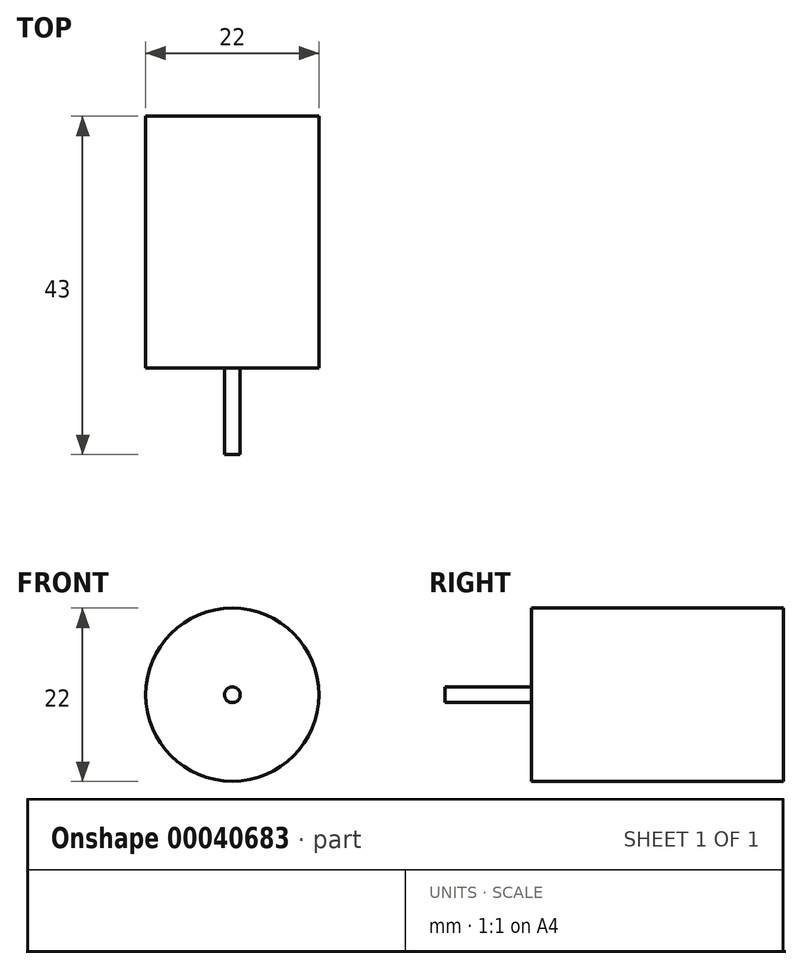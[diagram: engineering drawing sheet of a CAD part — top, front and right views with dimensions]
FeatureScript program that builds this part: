
annotation { "Feature Type Name" : "Feature", "Feature Type Description" : "" }
export const myFeature = defineFeature(function(context is Context, id is Id, definition is map)
    precondition{}
    {
        {
            var Q0;
            Q0=qCreatedBy(makeId("Front.planeOp"),FACE);
            var sketch = newSketch(context, id + "F0", { "sketchPlane" : qUnion([Q0])});
            skCircle(sketch, "E0", {"center": v(0, 0) * mm, "radius": 11 * mm});
            skSolve(sketch);
        }
        {
            var Q0;
            Q0=makeQuery(id+"F0.imprint","IMPRINT",FACE,{"disambiguationData":[TD([[makeQuery(id+"F0.imprint","IMPRINT",EDGE,{"derivedFrom":sQuery(id+"F0.wireOp",EDGE,"E0")}),1.0]])]});
            extrude(context, id + "F1", {"entities" : qUnion([Q0]), "oppositeDirection" : true, "depth" : 32 * mm});
        }
        {
            var Q0;
            Q0=makeQuery(id+"F1.opExtrude","CAP_FACE",FACE,{"disambiguationData":[OSD([sQuery(id+"F0.wireOp",EDGE,"E0")])],"isStart":true});
            var sketch = newSketch(context, id + "F2", { "sketchPlane" : qUnion([Q0])});
            skCircle(sketch, "E1", {"center": v(0, 0) * mm, "radius": 1 * mm});
            skSolve(sketch);
        }
        {
            var Q0;
            Q0 = qSketchRegion(id + "F2", true);
            extrude(context, id + "F3", {"entities" : qUnion([Q0]), "operationType" : NewBodyOperationType.ADD, "depth" : 11 * mm});
        }
    });
